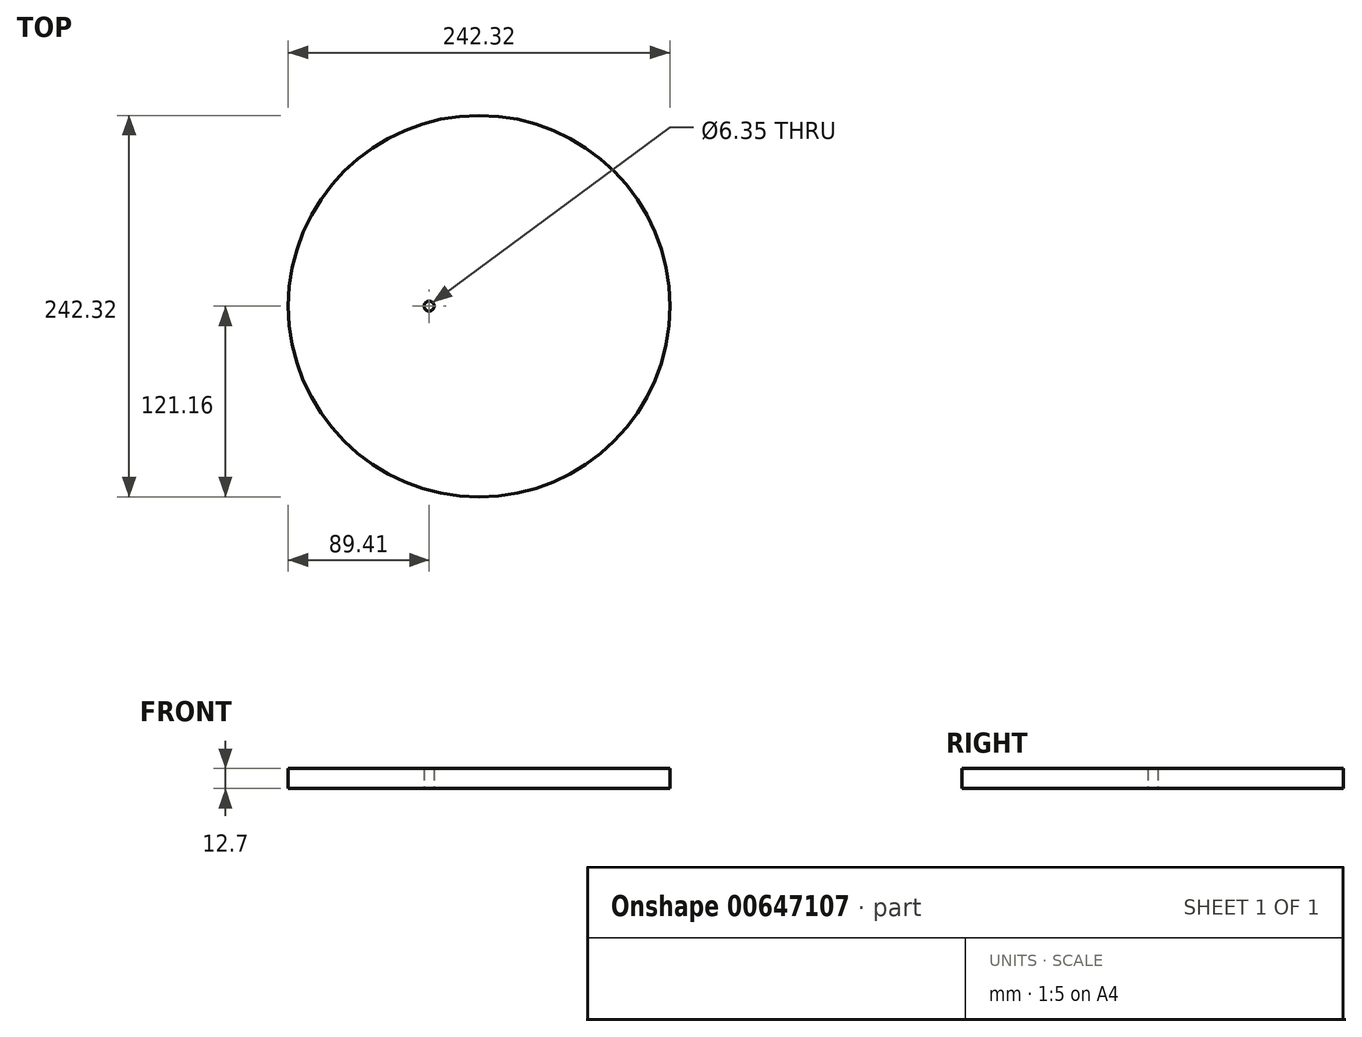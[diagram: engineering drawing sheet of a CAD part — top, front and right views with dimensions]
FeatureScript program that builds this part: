
annotation { "Feature Type Name" : "Feature", "Feature Type Description" : "" }
export const myFeature = defineFeature(function(context is Context, id is Id, definition is map)
    precondition{}
    {
        {
            var Q0;
            Q0=qCreatedBy(makeId("Top.planeOp"),FACE);
            var sketch = newSketch(context, id + "F0", { "sketchPlane" : qUnion([Q0])});
            skCircle(sketch, "E0", {"center": v(0, 0) * mm, "radius": 121.16 * mm});
            skCircle(sketch, "E1", {"center": v(-31.75, 0) * mm, "radius": 3.18 * mm});
            skSolve(sketch);
        }
        {
            var Q0;
            Q0=makeQuery(id+"F0.imprint","IMPRINT",FACE,{"disambiguationData":[TD([[makeQuery(id+"F0.imprint","IMPRINT",EDGE,{"derivedFrom":sQuery(id+"F0.wireOp",EDGE,"E0")}),1.0]])]});
            extrude(context, id + "F1", {"entities" : qUnion([Q0]), "depth" : 12.7 * mm, "offsetDistance" : 25.4 * mm});
        }
    });
